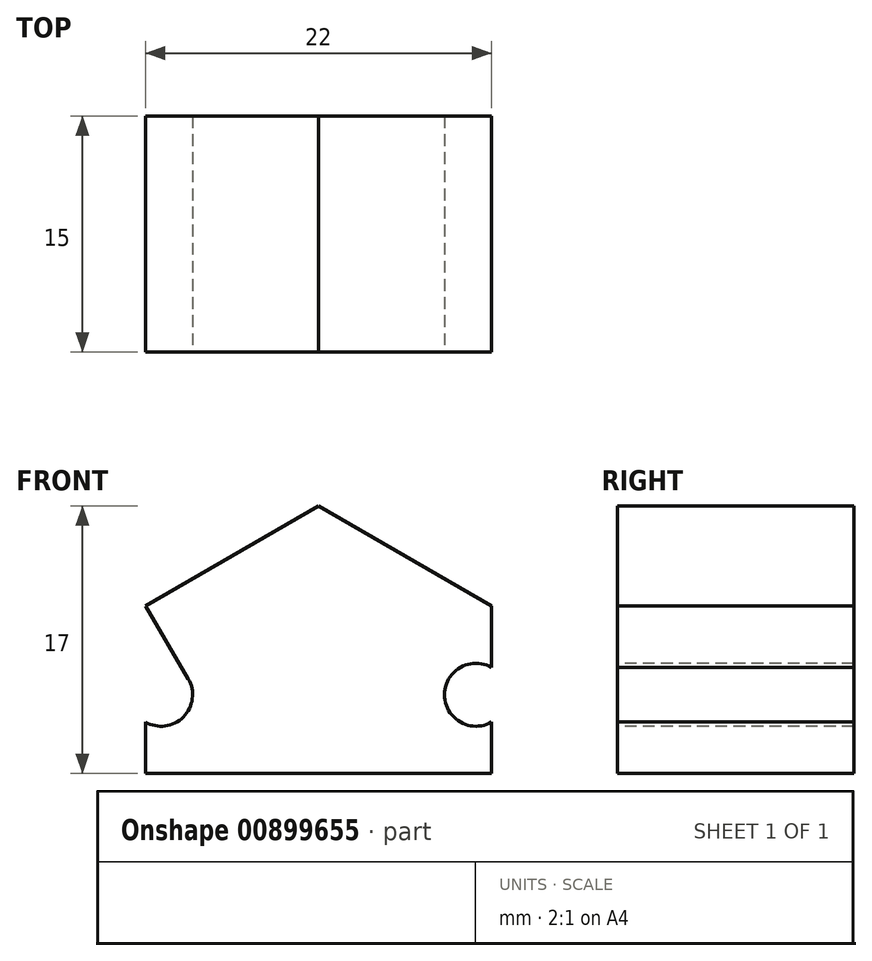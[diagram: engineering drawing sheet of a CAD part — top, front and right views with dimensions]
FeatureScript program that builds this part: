
annotation { "Feature Type Name" : "Feature", "Feature Type Description" : "" }
export const myFeature = defineFeature(function(context is Context, id is Id, definition is map)
    precondition{}
    {
        {
            var Q0;
            Q0=qCreatedBy(makeId("Front.planeOp"),FACE);
            var sketch = newSketch(context, id + "F0", { "sketchPlane" : qUnion([Q0])});
            skLineSegment(sketch, "E0.bottom", {"start": v(-4.54, 7.18) * mm, "end": v(17.46, 7.18) * mm});
            skLineSegment(sketch, "E0.top", {"start": v(-4.54, -9.82) * mm, "end": v(17.46, -9.82) * mm});
            skLineSegment(sketch, "E0.left", {"start": v(-4.54, 7.18) * mm, "end": v(-4.54, -9.82) * mm});
            skLineSegment(sketch, "E0.right", {"start": v(17.46, 7.18) * mm, "end": v(17.46, -9.82) * mm});
            skSolve(sketch);
        }
        {
            var Q0;
            Q0=makeQuery(id+"F0.imprint","IMPRINT",FACE,{"disambiguationData":[TD([[makeQuery(id+"F0.imprint","IMPRINT",EDGE,{"derivedFrom":sQuery(id+"F0.wireOp",EDGE,"E0.bottom")}),-1.0]])]});
            extrude(context, id + "F1", {"entities" : qUnion([Q0]), "depth" : 15 * mm, "offsetDistance" : 25 * mm});
        }
        {
            var Q0;
            Q0=makeQuery(id+"F1.opExtrude","CAP_FACE",FACE,{"disambiguationData":[OSD([sQuery(id+"F0.wireOp",EDGE,"E0.bottom"),sQuery(id+"F0.wireOp",EDGE,"E0.top"),sQuery(id+"F0.wireOp",EDGE,"E0.left"),sQuery(id+"F0.wireOp",EDGE,"E0.right")])],"isStart":false});
            var sketch = newSketch(context, id + "F2", { "sketchPlane" : qUnion([Q0])});
            skCircle(sketch, "E1", {"center": v(16.46, -4.82) * mm, "radius": 2 * mm});
            skCircle(sketch, "E2", {"center": v(-3.54, -4.82) * mm, "radius": 2 * mm});
            skSolve(sketch);
        }
        {
            var Q0;
            Q0 = qSketchRegion(id + "F2", true);
            extrude(context, id + "F3", {"entities" : qUnion([Q0]), "operationType" : NewBodyOperationType.REMOVE, "oppositeDirection" : true, "depth" : 33.7 * mm, "offsetDistance" : 25 * mm});
        }
        {
            var Q0;
            Q0=makeQuery(id+"F1.opExtrude","CAP_FACE",FACE,{"disambiguationData":[OSD([sQuery(id+"F0.wireOp",EDGE,"E0.bottom"),sQuery(id+"F0.wireOp",EDGE,"E0.top"),sQuery(id+"F0.wireOp",EDGE,"E0.left"),sQuery(id+"F0.wireOp",EDGE,"E0.right")])],"isStart":false});
            var sketch = newSketch(context, id + "F4", { "sketchPlane" : qUnion([Q0])});
            skLineSegment(sketch, "E3", {"start": v(6.46, 7.18) * mm, "end": v(-4.54, 0.83) * mm});
            skLineSegment(sketch, "E4", {"start": v(6.46, 7.18) * mm, "end": v(17.46, 0.83) * mm});
            skSolve(sketch);
        }
        {
            var Q0;
            {var subQ0=sQuery(id+"F4.wireOp",EDGE,"E3");Q0=makeQuery(id+"F4.imprint","IMPRINT",FACE,{"disambiguationData":[TD([[makeQuery(id+"F4.imprint","IMPRINT",EDGE,{"derivedFrom":subQ0}),-1.0]])]});}
            var Q1;
            {var subQ0=sQuery(id+"F4.wireOp",EDGE,"E4");Q1=makeQuery(id+"F4.imprint","IMPRINT",FACE,{"disambiguationData":[TD([[makeQuery(id+"F4.imprint","IMPRINT",EDGE,{"derivedFrom":subQ0}),1.0]])]});}
            extrude(context, id + "F5", {"entities" : qUnion([Q0, Q1]), "operationType" : NewBodyOperationType.REMOVE, "oppositeDirection" : true, "depth" : 25 * mm, "offsetDistance" : 25 * mm});
        }
        {
            var Q0;
            Q0=makeQuery(id+"F1.opExtrude","CAP_FACE",FACE,{"disambiguationData":[OSD([sQuery(id+"F0.wireOp",EDGE,"E0.bottom"),sQuery(id+"F0.wireOp",EDGE,"E0.top"),sQuery(id+"F0.wireOp",EDGE,"E0.left"),sQuery(id+"F0.wireOp",EDGE,"E0.right")])],"isStart":false});
            var sketch = newSketch(context, id + "F6", { "sketchPlane" : qUnion([Q0])});
            skLineSegment(sketch, "E5", {"start": v(17.46, 0.83) * mm, "end": v(14.91, -3.5) * mm});
            skLineSegment(sketch, "E6", {"start": v(-4.54, 0.83) * mm, "end": v(-1.82, -3.81) * mm});
            skSolve(sketch);
        }
        {
            var Q0;
            {var subQ0=sQuery(id+"F6.wireOp",EDGE,"E6");Q0=makeQuery(id+"F6.imprint","IMPRINT",FACE,{"disambiguationData":[TD([[makeQuery(id+"F6.imprint","IMPRINT",EDGE,{"derivedFrom":subQ0}),-1.0]])]});}
            extrude(context, id + "F7", {"entities" : qUnion([Q0]), "operationType" : NewBodyOperationType.REMOVE, "oppositeDirection" : true, "depth" : 25 * mm, "offsetDistance" : 25 * mm});
        }
    });
